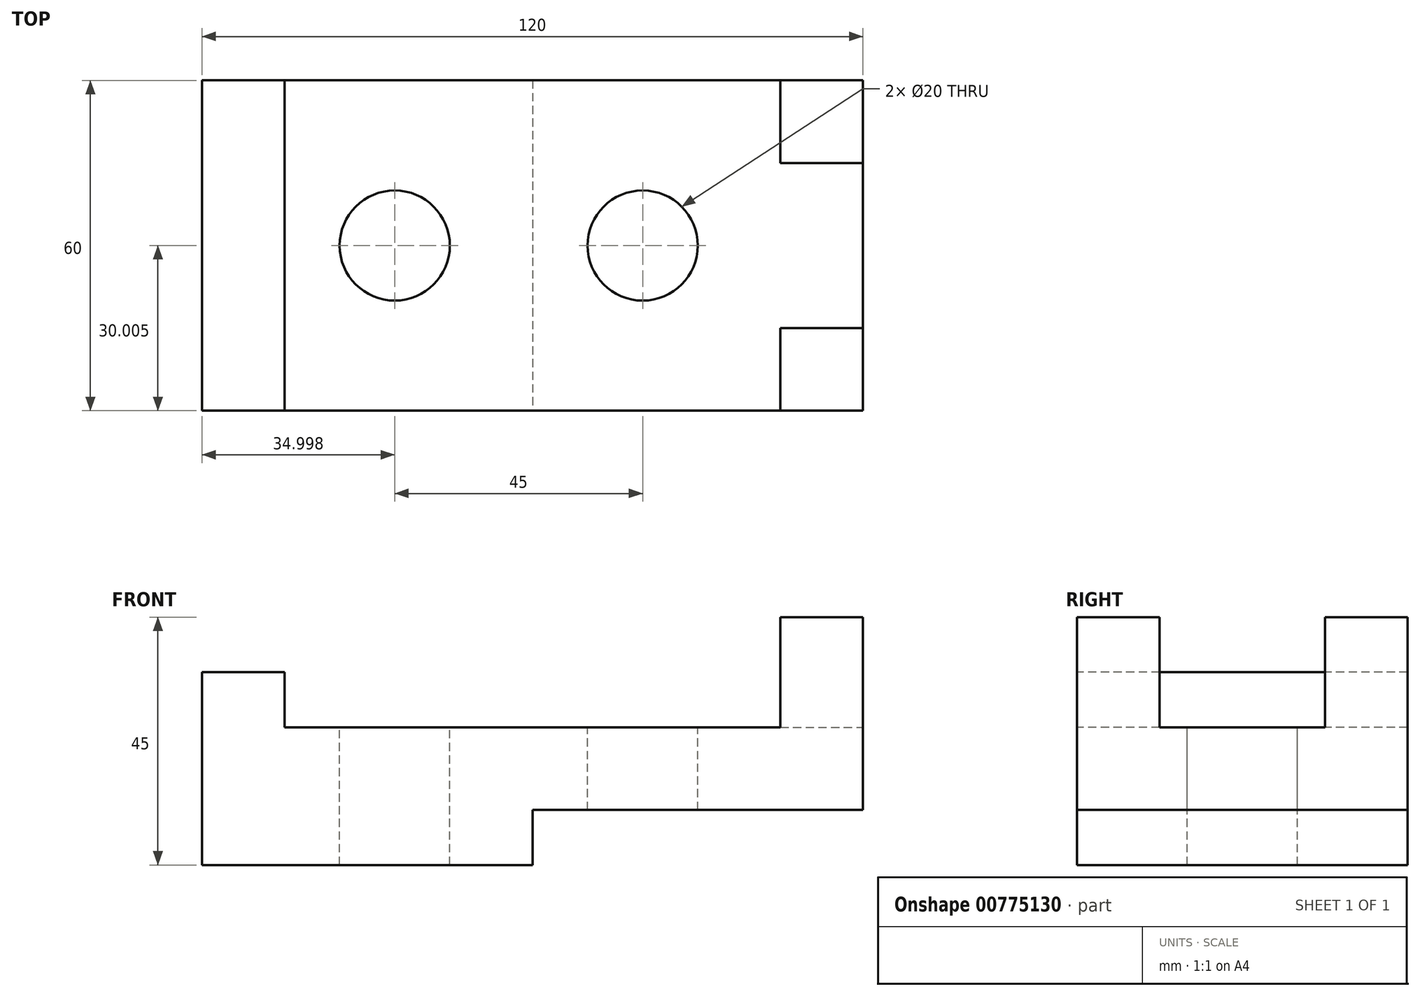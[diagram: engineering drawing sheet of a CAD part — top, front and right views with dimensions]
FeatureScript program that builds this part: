
annotation { "Feature Type Name" : "Feature", "Feature Type Description" : "" }
export const myFeature = defineFeature(function(context is Context, id is Id, definition is map)
    precondition{}
    {
        {
            var Q0;
            Q0=qCreatedBy(makeId("Top.planeOp"),FACE);
            var sketch = newSketch(context, id + "F0", { "sketchPlane" : qUnion([Q0])});
            skLineSegment(sketch, "E0.bottom", {"start": v(-83.56, 64.86) * mm, "end": v(36.44, 64.86) * mm});
            skLineSegment(sketch, "E0.top", {"start": v(-83.56, 4.86) * mm, "end": v(36.44, 4.86) * mm});
            skLineSegment(sketch, "E0.left", {"start": v(-83.56, 64.86) * mm, "end": v(-83.56, 4.86) * mm});
            skLineSegment(sketch, "E0.right", {"start": v(36.44, 64.86) * mm, "end": v(36.44, 4.86) * mm});
            skSolve(sketch);
        }
        {
            var Q0;
            Q0=makeQuery(id+"F0.imprint","IMPRINT",FACE,{"disambiguationData":[TD([[makeQuery(id+"F0.imprint","IMPRINT",EDGE,{"derivedFrom":sQuery(id+"F0.wireOp",EDGE,"E0.bottom")}),-1.0]])]});
            extrude(context, id + "F1", {"entities" : qUnion([Q0]), "depth" : 45 * mm, "offsetDistance" : 25 * mm});
        }
        {
            var Q0;
            Q0=makeQuery(id+"F1.opExtrude","SWEPT_FACE",FACE,{"disambiguationData":[OSD([sQuery(id+"F0.wireOp",EDGE,"E0.top")])]});
            var sketch = newSketch(context, id + "F2", { "sketchPlane" : qUnion([Q0])});
            skLineSegment(sketch, "E1.bottom", {"start": v(36.44, 0) * mm, "end": v(-23.56, 0) * mm});
            skLineSegment(sketch, "E1.top", {"start": v(36.44, 10) * mm, "end": v(-23.56, 10) * mm});
            skLineSegment(sketch, "E1.left", {"start": v(36.44, 0) * mm, "end": v(36.44, 10) * mm});
            skLineSegment(sketch, "E1.right", {"start": v(-23.56, 0) * mm, "end": v(-23.56, 10) * mm});
            skPoint(sketch, "E2", {"position": v(21.44, 45) * mm});
            skPoint(sketch, "E3", {"position": v(21.44, 25) * mm});
            skLineSegment(sketch, "E4", {"start": v(-83.56, 45) * mm, "end": v(-83.56, 35) * mm, "construction": true});
            skLineSegment(sketch, "E5", {"start": v(-83.56, 35) * mm, "end": v(-68.56, 35) * mm});
            skLineSegment(sketch, "E6", {"start": v(-68.56, 35) * mm, "end": v(-68.56, 25) * mm});
            skLineSegment(sketch, "E7", {"start": v(-68.56, 25) * mm, "end": v(21.44, 25) * mm});
            skLineSegment(sketch, "E8", {"start": v(21.44, 25) * mm, "end": v(21.44, 45) * mm});
            skLineSegment(sketch, "E9", {"start": v(-83.56, 45) * mm, "end": v(21.44, 45) * mm});
            skSolve(sketch);
        }
        {
            var Q0;
            {var subQ0=sQuery(id+"F2.wireOp",EDGE,"E5");Q0=makeQuery(id+"F2.imprint","IMPRINT",FACE,{"disambiguationData":[TD([[makeQuery(id+"F2.imprint","IMPRINT",EDGE,{"derivedFrom":subQ0}),1.0]])]});}
            var Q1;
            Q1=makeQuery(id+"F2.imprint","IMPRINT",FACE,{"disambiguationData":[TD([[makeQuery(id+"F2.imprint","IMPRINT",EDGE,{"derivedFrom":sQuery(id+"F2.wireOp",EDGE,"E1.bottom")}),1.0]])]});
            extrude(context, id + "F3", {"entities" : qUnion([Q0, Q1]), "operationType" : NewBodyOperationType.REMOVE, "oppositeDirection" : true, "depth" : 60 * mm, "offsetDistance" : 25 * mm});
        }
        {
            var Q0;
            Q0=makeQuery(id+"F1.opExtrude","SWEPT_FACE",FACE,{"disambiguationData":[OSD([sQuery(id+"F0.wireOp",EDGE,"E0.right")])]});
            var sketch = newSketch(context, id + "F4", { "sketchPlane" : qUnion([Q0])});
            skLineSegment(sketch, "E10", {"start": v(19.86, 45) * mm, "end": v(19.86, 25) * mm});
            skLineSegment(sketch, "E11", {"start": v(19.86, 25) * mm, "end": v(49.86, 25) * mm});
            skLineSegment(sketch, "E12", {"start": v(49.86, 25) * mm, "end": v(49.86, 45) * mm});
            skLineSegment(sketch, "E13", {"start": v(49.86, 45) * mm, "end": v(19.86, 45) * mm});
            skSolve(sketch);
        }
        {
            var Q0;
            Q0=makeQuery(id+"F4.imprint","IMPRINT",FACE,{"disambiguationData":[TD([[makeQuery(id+"F4.imprint","IMPRINT",EDGE,{"derivedFrom":sQuery(id+"F4.wireOp",EDGE,"E10")}),1.0]])]});
            extrude(context, id + "F5", {"entities" : qUnion([Q0]), "operationType" : NewBodyOperationType.REMOVE, "oppositeDirection" : true, "depth" : 15 * mm, "offsetDistance" : 25 * mm});
        }
        {
            var Q0;
            Q0=makeQuery(id+"F5.boolean.opBoolean","MERGE",FACE,{"derivedFrom":[makeQuery(id+"F3.boolean.opBoolean","COPY",FACE,{"derivedFrom":makeQuery(id+"F3.opExtrude","SWEPT_FACE",FACE,{"disambiguationData":[OSD([sQuery(id+"F2.wireOp",EDGE,"E7")])]})}),makeQuery(id+"F5.opExtrude","SWEPT_FACE",FACE,{"disambiguationData":[OSD([sQuery(id+"F4.wireOp",EDGE,"E11")])]})]});
            var sketch = newSketch(context, id + "F6", { "sketchPlane" : qUnion([Q0])});
            skCircle(sketch, "E14", {"center": v(-48.56, 34.86) * mm, "radius": 10 * mm});
            skCircle(sketch, "E15", {"center": v(-3.56, 34.86) * mm, "radius": 10 * mm});
            skSolve(sketch);
        }
        {
            var Q0;
            Q0=makeQuery(id+"F6.imprint","IMPRINT",FACE,{"disambiguationData":[TD([[makeQuery(id+"F6.imprint","IMPRINT",EDGE,{"derivedFrom":sQuery(id+"F6.wireOp",EDGE,"E14")}),1.0]])]});
            var Q1;
            Q1=makeQuery(id+"F6.imprint","IMPRINT",FACE,{"disambiguationData":[TD([[makeQuery(id+"F6.imprint","IMPRINT",EDGE,{"derivedFrom":sQuery(id+"F6.wireOp",EDGE,"E15")}),1.0]])]});
            extrude(context, id + "F7", {"entities" : qUnion([Q0, Q1]), "operationType" : NewBodyOperationType.REMOVE, "oppositeDirection" : true, "depth" : 25 * mm, "offsetDistance" : 25 * mm});
        }
    });
